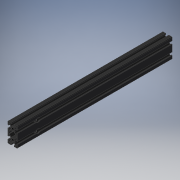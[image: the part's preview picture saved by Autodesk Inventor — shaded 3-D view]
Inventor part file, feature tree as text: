
AUTODESK INVENTOR PART (.ipt)
format: ipt  version: 2019 (Build 230136000, 136)  size: 347,136 bytes
history: native  units: mm
features: other x8, sketch x5, hole x3, pattern_linear x3, revolve x2, extrude x1
ambient origin geometry x8: Origin, YZ Plane, XZ Plane, XY Plane, X Axis, Y Axis, Z Axis, Center Point
bodies: Solid1 (feature_tree)
feature tree (22):
  extrude  "Extrusion1"  Depth=20.0mm TaperAngle=0.0deg
  hole  "Hole1"  [1 undecoded]
  pattern_linear  "Rectangular Pattern1"  Count1=2 Spacing1=10.0mm
  hole  "Hole2"  [1 undecoded]
  pattern_linear  "Rectangular Pattern2"  Spacing1=0.0mm  [1 undecoded]
  hole  "Hole3"  [1 undecoded]
  pattern_linear  "Rectangular Pattern3"  [2 undecoded]
  revolve  "Revolution1"  [1 undecoded]
  revolve  "Revolution2"  [1 undecoded]
  other  "C1_XY"
  other  "C1_YZ"
  other  "C1_ZX"
  other  "C1_X"
  other  "C1_Y"
  other  "C1_Z"
  other  "C1_Center"
  sketch  "Sketch_1"  dims[d0=320.0mm d1=0.0mm]
  sketch  "Sketch2"  dims[d2=4.134mm d3=15.0mm d4=5.0mm d5=2.0mm d6=90.0deg d7=15.0mm d8=0.0mm d9=20.0mm d11=20.0mm d12=10.0mm d14=0.0mm]
  sketch  "Sketch3"  dims[d15=4.134mm d16=15.0mm d17=5.0mm d18=2.0mm d19=90.0deg d20=15.0mm d21=0.0mm d22=20.0mm d24=20.0mm d25=10.0mm d27=0.0mm]
  sketch  "Sketch4"  dims[d28=4.2mm d29=6.0mm d30=4.0mm d31=2.0mm d32=90.0deg d33=290.0mm d34=0.0mm d35=20.0mm d37=20.0mm d38=10.0mm d40=0.0mm]
  sketch  "Sketch_50"  dims[d41=360.0deg d42=360.0deg d43=0.0mm]
  other  "_p_______27_Sketch_50_0"
note: 8 required parameter values undecoded (feature->parameter linkage not recoverable at this tier; creation-order binding heuristic only, values carry confidence <= 0.55)
